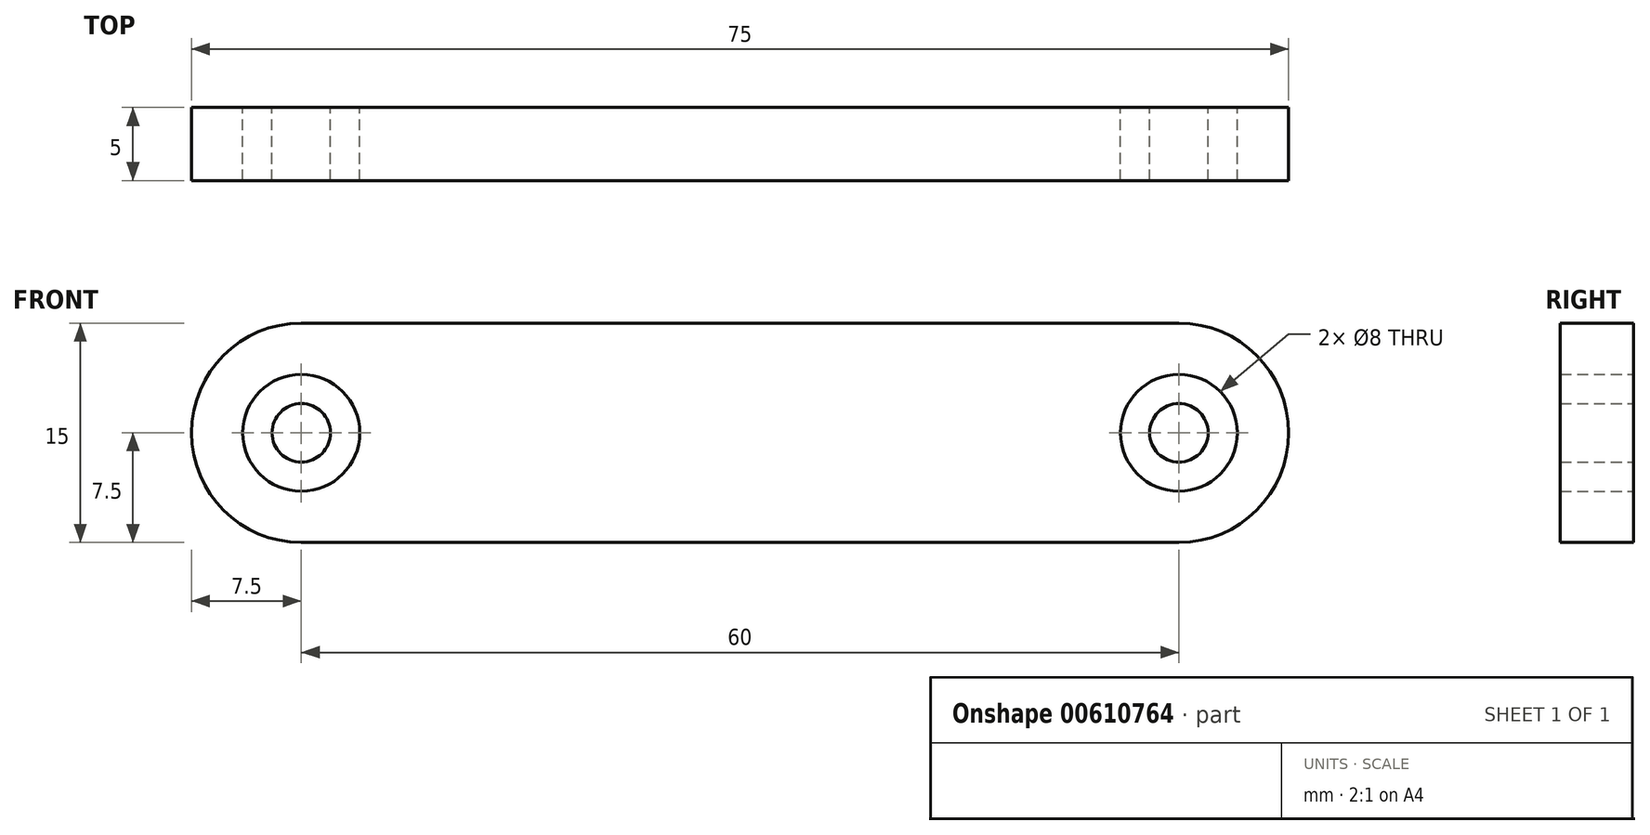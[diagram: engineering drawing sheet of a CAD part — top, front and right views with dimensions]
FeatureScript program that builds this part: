
annotation { "Feature Type Name" : "Feature", "Feature Type Description" : "" }
export const myFeature = defineFeature(function(context is Context, id is Id, definition is map)
    precondition{}
    {
        {
            var Q0;
            Q0=qCreatedBy(makeId("Front.planeOp"),FACE);
            var sketch = newSketch(context, id + "F0", { "sketchPlane" : qUnion([Q0])});
            skArc(sketch, "E0", {"start": v(0, 7.5) * mm, "mid": v(-7.5, 0) * mm, "end": v(0, -7.5) * mm});
            skArc(sketch, "E1", {"start": v(60, -7.5) * mm, "mid": v(67.5, 0) * mm, "end": v(60, 7.5) * mm});
            skLineSegment(sketch, "E2", {"start": v(0, 7.5) * mm, "end": v(60, 7.5) * mm});
            skLineSegment(sketch, "E3", {"start": v(0, -7.5) * mm, "end": v(60, -7.5) * mm});
            skLineSegment(sketch, "E4", {"start": v(60, 7.5) * mm, "end": v(60, -7.5) * mm, "construction": true});
            skCircle(sketch, "E5", {"center": v(0, 0) * mm, "radius": 4 * mm});
            skCircle(sketch, "E6", {"center": v(60, 0) * mm, "radius": 4 * mm});
            skSolve(sketch);
        }
        {
            var Q0;
            Q0 = qSketchRegion(id + "F0", true);
            extrude(context, id + "F1", {"entities" : qUnion([Q0]), "depth" : 5 * mm, "offsetDistance" : 25.4 * mm});
        }
        {
            var Q0;
            Q0=qCreatedBy(makeId("Front.planeOp"),FACE);
            var sketch = newSketch(context, id + "F2", { "sketchPlane" : qUnion([Q0])});
            skCircle(sketch, "E7", {"center": v(0, 0) * mm, "radius": 2 * mm});
            skLineSegment(sketch, "E8", {"start": v(60, 11.13) * mm, "end": v(60, -12.64) * mm, "construction": true});
            skCircle(sketch, "E9", {"center": v(60, 0) * mm, "radius": 2 * mm});
            skSolve(sketch);
        }
        {
            var Q0;
            Q0 = qSketchRegion(id + "F2", true);
            extrude(context, id + "F3", {"entities" : qUnion([Q0]), "depth" : 5 * mm, "offsetDistance" : 25.4 * mm});
        }
    });
